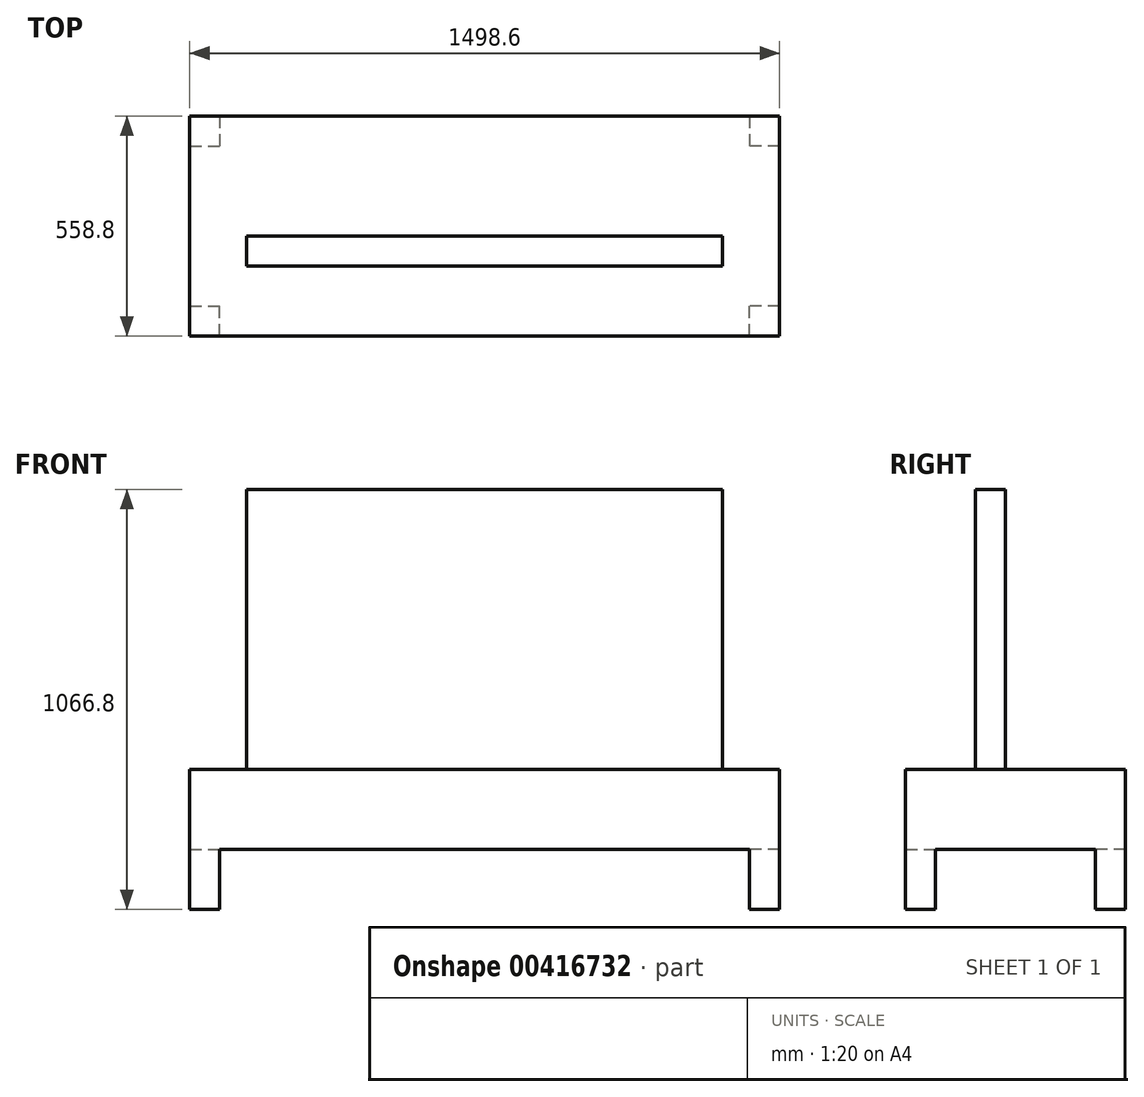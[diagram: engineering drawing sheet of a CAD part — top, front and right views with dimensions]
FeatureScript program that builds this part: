
annotation { "Feature Type Name" : "Feature", "Feature Type Description" : "" }
export const myFeature = defineFeature(function(context is Context, id is Id, definition is map)
    precondition{}
    {
        {
            var Q0;
            Q0=qCreatedBy(makeId("Top.planeOp"),FACE);
            var sketch = newSketch(context, id + "F0", { "sketchPlane" : qUnion([Q0])});
            skLineSegment(sketch, "E0.bottom", {"start": v(0, 0) * mm, "end": v(1498.6, 0) * mm, "construction": true});
            skLineSegment(sketch, "E0.top", {"start": v(0, 558.8) * mm, "end": v(1498.6, 558.8) * mm, "construction": true});
            skLineSegment(sketch, "E0.left", {"start": v(0, 0) * mm, "end": v(0, 558.8) * mm, "construction": true});
            skLineSegment(sketch, "E0.right", {"start": v(1498.6, 0) * mm, "end": v(1498.6, 558.8) * mm, "construction": true});
            skLineSegment(sketch, "E1.bottom", {"start": v(0, 0) * mm, "end": v(76.2, 0) * mm});
            skLineSegment(sketch, "E1.top", {"start": v(0, 76.2) * mm, "end": v(76.2, 76.2) * mm});
            skLineSegment(sketch, "E1.left", {"start": v(0, 0) * mm, "end": v(0, 76.2) * mm});
            skLineSegment(sketch, "E1.right", {"start": v(76.2, 0) * mm, "end": v(76.2, 76.2) * mm});
            skLineSegment(sketch, "E2.bottom", {"start": v(0, 558.8) * mm, "end": v(76.2, 558.8) * mm});
            skLineSegment(sketch, "E2.top", {"start": v(0, 482.6) * mm, "end": v(76.2, 482.6) * mm});
            skLineSegment(sketch, "E2.left", {"start": v(0, 558.8) * mm, "end": v(0, 482.6) * mm});
            skLineSegment(sketch, "E2.right", {"start": v(76.2, 558.8) * mm, "end": v(76.2, 482.6) * mm});
            skLineSegment(sketch, "E3.bottom", {"start": v(1498.6, 558.8) * mm, "end": v(1422.4, 558.8) * mm});
            skLineSegment(sketch, "E3.top", {"start": v(1498.6, 482.6) * mm, "end": v(1422.4, 482.6) * mm});
            skLineSegment(sketch, "E3.left", {"start": v(1498.6, 558.8) * mm, "end": v(1498.6, 482.6) * mm});
            skLineSegment(sketch, "E3.right", {"start": v(1422.4, 558.8) * mm, "end": v(1422.4, 482.6) * mm});
            skLineSegment(sketch, "E4.bottom", {"start": v(1498.6, 0) * mm, "end": v(1422.4, 0) * mm});
            skLineSegment(sketch, "E4.top", {"start": v(1498.6, 76.2) * mm, "end": v(1422.4, 76.2) * mm});
            skLineSegment(sketch, "E4.left", {"start": v(1498.6, 0) * mm, "end": v(1498.6, 76.2) * mm});
            skLineSegment(sketch, "E4.right", {"start": v(1422.4, 0) * mm, "end": v(1422.4, 76.2) * mm});
            skSolve(sketch);
        }
        {
            var Q0;
            Q0=makeQuery(id+"F0.imprint","IMPRINT",FACE,{"disambiguationData":[TD([[makeQuery(id+"F0.imprint","IMPRINT",EDGE,{"derivedFrom":sQuery(id+"F0.wireOp",EDGE,"E1.bottom")}),1.0]])]});
            extrude(context, id + "F1", {"entities" : qUnion([Q0]), "depth" : 152.4 * mm});
        }
        {
            var Q0;
            Q0=makeQuery(id+"F0.imprint","IMPRINT",FACE,{"disambiguationData":[TD([[makeQuery(id+"F0.imprint","IMPRINT",EDGE,{"derivedFrom":sQuery(id+"F0.wireOp",EDGE,"E2.bottom")}),-1.0]])]});
            var Q1;
            Q1=makeQuery(id+"F0.imprint","IMPRINT",FACE,{"disambiguationData":[TD([[makeQuery(id+"F0.imprint","IMPRINT",EDGE,{"derivedFrom":sQuery(id+"F0.wireOp",EDGE,"E3.bottom")}),1.0]])]});
            var Q2;
            Q2=makeQuery(id+"F0.imprint","IMPRINT",FACE,{"disambiguationData":[TD([[makeQuery(id+"F0.imprint","IMPRINT",EDGE,{"derivedFrom":sQuery(id+"F0.wireOp",EDGE,"E4.bottom")}),-1.0]])]});
            extrude(context, id + "F2", {"entities" : qUnion([Q0, Q1, Q2]), "operationType" : NewBodyOperationType.ADD, "depth" : 152.4 * mm});
        }
        {
            var Q0;
            Q0=makeQuery(id+"F1.opExtrude","CAP_FACE",FACE,{"disambiguationData":[OSD([sQuery(id+"F0.wireOp",EDGE,"E1.bottom"),sQuery(id+"F0.wireOp",EDGE,"E1.top"),sQuery(id+"F0.wireOp",EDGE,"E1.left"),sQuery(id+"F0.wireOp",EDGE,"E1.right")])],"isStart":false});
            var sketch = newSketch(context, id + "F3", { "sketchPlane" : qUnion([Q0])});
            skLineSegment(sketch, "E5.bottom", {"start": v(0, 0) * mm, "end": v(1498.6, 0) * mm});
            skLineSegment(sketch, "E5.top", {"start": v(0, 558.8) * mm, "end": v(1498.6, 558.8) * mm});
            skLineSegment(sketch, "E5.left", {"start": v(0, 0) * mm, "end": v(0, 558.8) * mm});
            skLineSegment(sketch, "E5.right", {"start": v(1498.6, 0) * mm, "end": v(1498.6, 558.8) * mm});
            skPoint(sketch, "E6.0", {"position": v(1498.6, 558.8) * mm});
            skSolve(sketch);
        }
        {
            var Q0;
            {var subQ2=sQuery(id+"F3.wireOp",EDGE,"E5.top");Q0=makeQuery(id+"F3.imprint","IMPRINT",FACE,{"disambiguationData":[TD([[makeQuery(id+"F3.imprint","IMPRINT",EDGE,{"derivedFrom":subQ2}),-1.0]])]});}
            var Q1;
            {var subQ4=makeQuery(id+"F1.opExtrude","CAP_EDGE",EDGE,{"disambiguationData":[OSD([sQuery(id+"F0.wireOp",EDGE,"E1.top")])],"isStart":false});Q1=makeQuery(id+"F3.imprint","IMPRINT",FACE,{"disambiguationData":[TD([[makeQuery(id+"F3.imprint","IMPRINT",EDGE,{"derivedFrom":subQ4}),-1.0]])]});}
            extrude(context, id + "F4", {"entities" : qUnion([Q0, Q1]), "operationType" : NewBodyOperationType.ADD, "depth" : 203.2 * mm});
        }
        {
            var Q0;
            Q0=makeQuery(id+"F4.opExtrude","CAP_FACE",FACE,{"disambiguationData":[OSD([sQuery(id+"F3.wireOp",EDGE,"E5.bottom"),sQuery(id+"F3.wireOp",EDGE,"E5.top"),sQuery(id+"F3.wireOp",EDGE,"E5.left"),sQuery(id+"F3.wireOp",EDGE,"E5.right")])],"isStart":false});
            var sketch = newSketch(context, id + "F5", { "sketchPlane" : qUnion([Q0])});
            skLineSegment(sketch, "E7.bottom", {"start": v(144.78, 254) * mm, "end": v(1353.82, 254) * mm});
            skLineSegment(sketch, "E7.top", {"start": v(144.78, 177.8) * mm, "end": v(1353.82, 177.8) * mm});
            skLineSegment(sketch, "E7.left", {"start": v(144.78, 254) * mm, "end": v(144.78, 177.8) * mm});
            skLineSegment(sketch, "E7.right", {"start": v(1353.82, 254) * mm, "end": v(1353.82, 177.8) * mm});
            skLineSegment(sketch, "E8", {"start": v(749.3, 558.8) * mm, "end": v(749.3, 254) * mm, "construction": true});
            skSolve(sketch);
        }
        {
            var Q0;
            Q0=makeQuery(id+"F5.imprint","IMPRINT",FACE,{"disambiguationData":[TD([[makeQuery(id+"F5.imprint","IMPRINT",EDGE,{"derivedFrom":sQuery(id+"F5.wireOp",EDGE,"E7.bottom")}),-1.0]])]});
            extrude(context, id + "F6", {"entities" : qUnion([Q0]), "operationType" : NewBodyOperationType.ADD, "depth" : 711.2 * mm});
        }
    });
